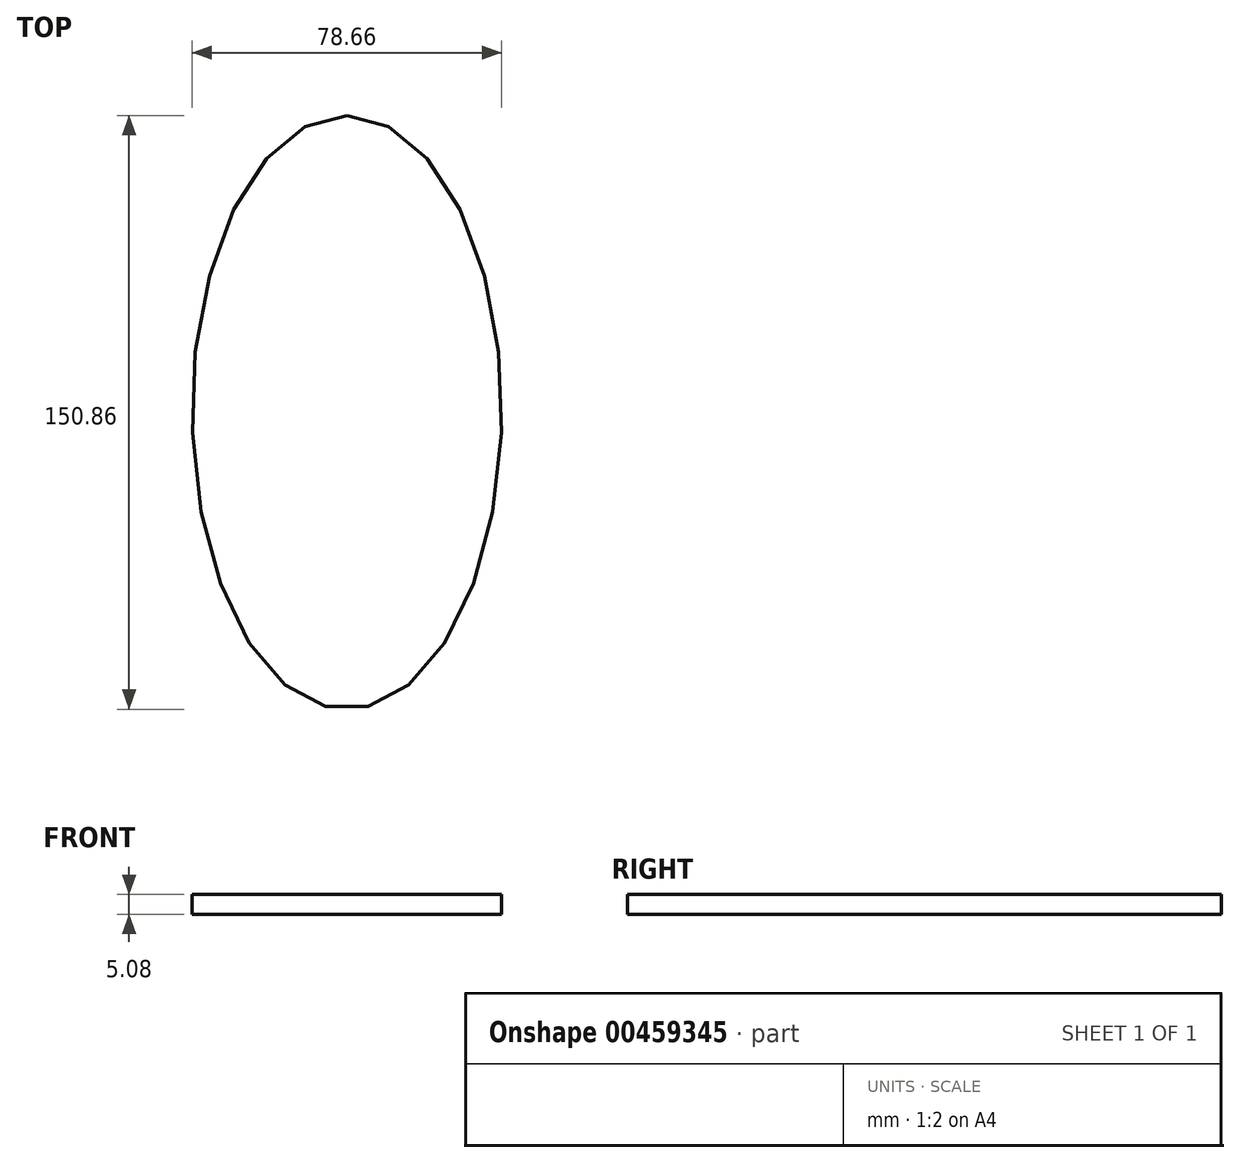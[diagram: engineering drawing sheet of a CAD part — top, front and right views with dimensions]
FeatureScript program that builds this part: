
annotation { "Feature Type Name" : "Feature", "Feature Type Description" : "" }
export const myFeature = defineFeature(function(context is Context, id is Id, definition is map)
    precondition{}
    {
        {
            var Q0;
            Q0=qCreatedBy(makeId("Top.planeOp"),FACE);
            var sketch = newSketch(context, id + "F0", { "sketchPlane" : qUnion([Q0])});
            skEllipse(sketch, "E0", {"center": v(0, 0) * mm, "majorRadius": 75.43 * mm, "minorRadius": 39.33 * mm, "majorAxis": v(0, 1)});
            skSolve(sketch);
        }
        {
            var Q0;
            Q0=makeQuery(id+"F0.imprint","IMPRINT",FACE,{"disambiguationData":[TD([[makeQuery(id+"F0.imprint","IMPRINT",EDGE,{"derivedFrom":sQuery(id+"F0.wireOp",EDGE,"E0")}),1.0]])]});
            extrude(context, id + "F1", {"entities" : qUnion([Q0]), "depth" : 5.08 * mm});
        }
    });
